# Revit family: ZETA_Коробка_Клемная_КМ 43-10_IP43
name_source: partatom
category: Электрические приборы
units: mm (PartAtom-declared; Revit-internal decimal feet)

## family parameters
Всегда вертикально = Нет
На основе рабочей плоскости = Да
Общий = Нет
При загрузке вырезать с полостями = Нет
Размер круглого соединителя = Использовать диаметр
Сохранять ориентацию аннотаций = Нет
Тип детали = Нормальный
Точка принадлежности помещению = Да

## types (1)
- 43-10_IP43
    ADSK_URL документации изделия = https://nzeta.ru
    ADSK_URL страницы изделия = https://nzeta.ru
    ADSK_Версия Revit = 2021
    ADSK_Версия семейства = v.1
    ADSK_Единица измерения = шт
    ADSK_Завод-изготовитель = АО «ЗЭТА»
    ADSK_Классификация нагрузок = Прочее
    ADSK_Код изделия = zeta30338
    ADSK_Количество = 1
    ADSK_Количество фаз = 1
    ADSK_Количество фаз числовое = 1
    ADSK_Коэффициент мощности = 1
    ADSK_Марка = KK КМ 43-10 У3 IP43
    ADSK_Масса = 1.1
    ADSK_Масса_Текст = 1,1
    ADSK_Материал наименование = Сталь оцинкованная
    ADSK_Наименование = Коробка монтажная КМ 43-10 У3 IP43 ступенчатый ПВХ ввод ГОФРОМАТИК
    ADSK_Наименование краткое = КМ 43-10
    ADSK_Напряжение = 230 В
    ADSK_Номер линии = 0
    ADSK_Номинальная мощность = 0 Вт
    ADSK_Обозначение = KK
    ADSK_Полная мощность = 0 В·А
    ADSK_Размер_Высота = 100 мм
    ADSK_Размер_Длина = 215 мм
    ADSK_Размер_Ширина = 175 мм
    ADSK_Степень защиты_IP = IP43
    ADSK_Ток = 0 А
    D1 = 25 мм
    D2 = 32 мм
    URL = https://nzeta.ru
    Изготавливается по = ТУ 27.33.13.120-047-99856433-2020
    Изготовитель = АО «ЗЭТА»
    Климатическое исполнение = У3
    Крышка_Длина = 190 мм
    Крышка_Ширина = 160 мм
    Напряжение переменного тока = 660 В
    Напряжение постоянного тока = 440 В
    Номинальный ток = до 25A
    Описание = Коробки клеммные соединительные КМ43 и КМ65 предназначены для
соединения и разветвления силовых электрических цепей и цепей КИПиА,
выполняемых контрольными и силовыми кабелями с алюминиевыми или медными
жилами сечением 1,5-4мм2.
    Отметка по умолчанию = 1219 мм
    Сертификат = RU C-RU.АД84.В.00192/20
    Сечение жил до = 4мм2
    Температура эксплуатации = от -40°С до +60°С
    УГО_Высота = 5 мм
    УГО_Ширина = 10 мм

## geometry (parser evidence)
native form markers: Sweep x1
no freeform markers — native parametric forms only
